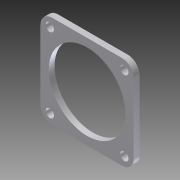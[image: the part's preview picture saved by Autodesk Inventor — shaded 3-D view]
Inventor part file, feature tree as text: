
AUTODESK INVENTOR PART (.ipt)
format: ipt  version: 2012 (Build 160160000, 160)  size: 156,672 bytes
history: native  units: in
note: dims shown in document units (in); Inventor stores cm internally (conversion verified against a paired STEP export)
features: extrude x2, fillet x2, sketch x1, hole x1
ambient origin geometry x8: Origin, YZ Plane, XZ Plane, XY Plane, X Axis, Y Axis, Z Axis, Center Point
bodies: Solid1 (feature_tree)
feature tree (6):
  sketch  "Sketch1"  dims[d0=0.9449in d1=0.4724in d2=1.0236in d3=0.5118in d4=0.0787in d5=0.2559in d6=0.128in d7=0.0787in d8=0.5625in d9=2.0in d10=1.0in d11=2.0in d12=1.0in d13=0.1181in d14=0.3937in d15=0.1575in d16=0.1575in d17=0.1575in d18=0.1575in d19=0.1575in d20=0.2in d21=0.2in d22=0.2in d23=0.2in d24=0.125in d25=0.0in d26=0.125in d27=0.18in d28=0.75in d29=0.27in d30=0.2in d31=0.5635in d32=1.0in d33=0.8108in d34=1.6in d35=1.6in d44=1.645in d45=0.125in d46=0.125in d47=0.125in d48=1.5in d49=1.5in d50=1.5in d51=1.5in d53=1.7321in d54=1.0in d55=0.0in d56=0.25in]
  extrude  "Extrusion1"  Depth=0.4724in
  fillet  "Fillet1"  Radius=1.0236in
  hole  "Hole1"  [1 undecoded]
  extrude  "Extrusion2"  Depth=0.0787in
  fillet  "Fillet2"  Radius=0.2559in
note: 1 required parameter value undecoded (feature->parameter linkage not recoverable at this tier; creation-order binding heuristic only, values carry confidence <= 0.55)
